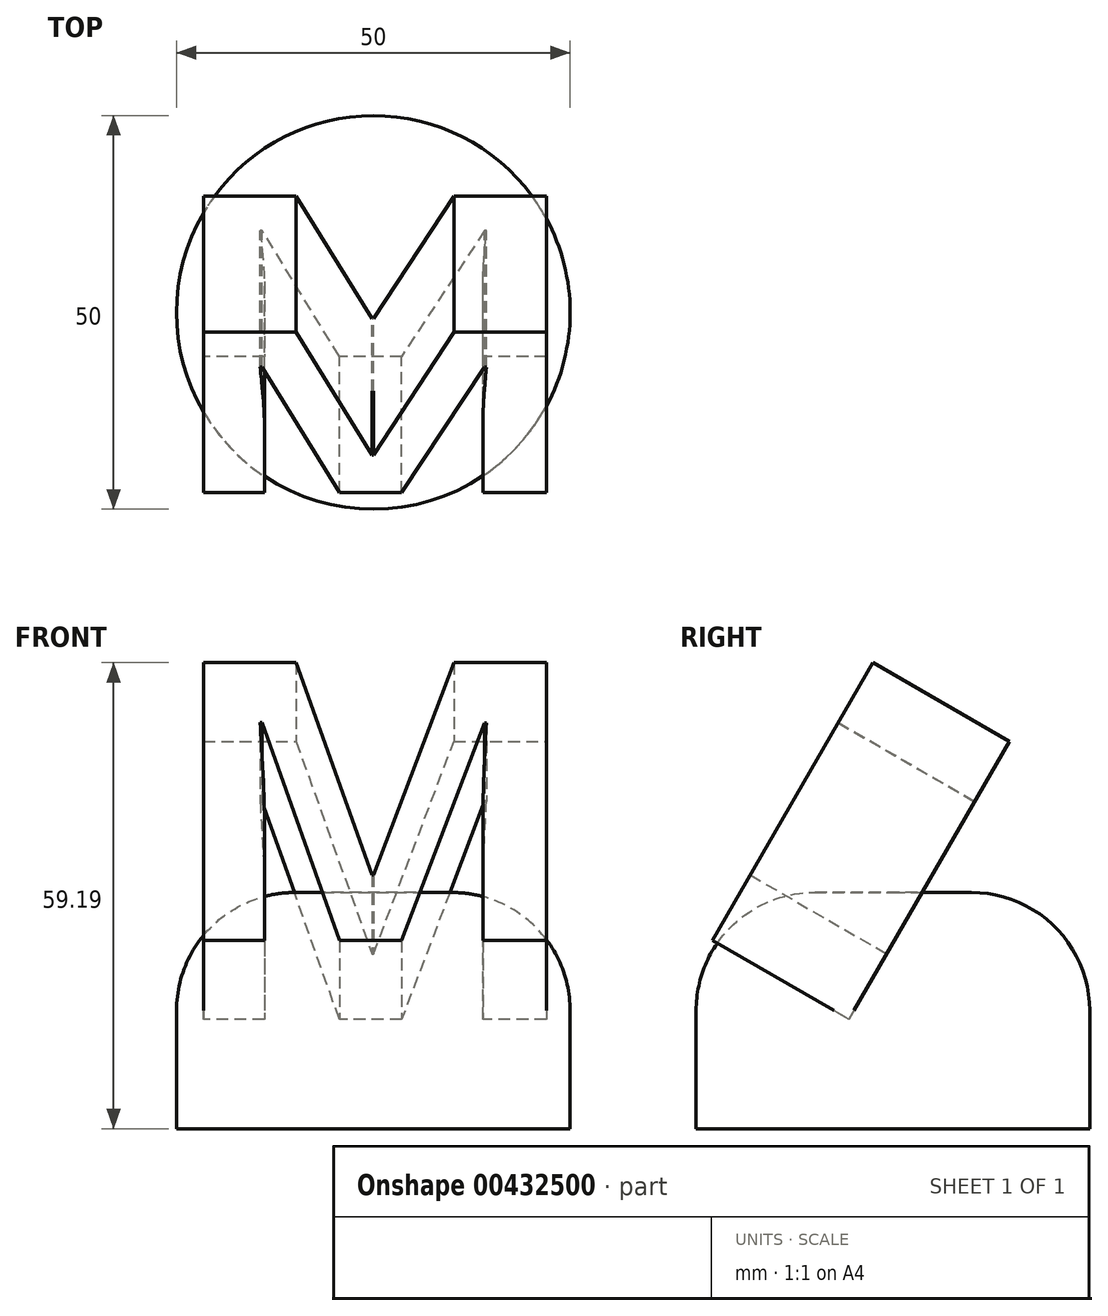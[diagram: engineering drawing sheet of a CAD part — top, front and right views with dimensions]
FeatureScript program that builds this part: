
annotation { "Feature Type Name" : "Feature", "Feature Type Description" : "" }
export const myFeature = defineFeature(function(context is Context, id is Id, definition is map)
    precondition{}
    {
        {
            var Q0;
            Q0=qCreatedBy(makeId("Top.planeOp"),FACE);
            var sketch = newSketch(context, id + "F0", { "sketchPlane" : qUnion([Q0])});
            skText(sketch, "E0", { "text": "M", "fontName": "OpenSans-Bold.ttf"});
            const initialGuessF0  = {"E0": [-0.09905, -0.02287, 1, 0, 0.0411]};
            skSetInitialGuess(sketch, initialGuessF0);
            skSolve(sketch);
        }
        {
            var Q0;
            Q0=qSketchRegion(id+"F0",true);
            extrude(context, id + "F1", {"entities" : qUnion([Q0]), "depth" : 20 * mm});
        }
        {
            var Q0;
            Q0=makeQuery(id+"F1.opExtrude","SWEPT_BODY",BODY,{"disambiguationData":[OSD([sQuery(id+"F0.wireOp",EDGE,"E0.sketch_text.stroke-0"),sQuery(id+"F0.wireOp",EDGE,"E0.sketch_text.stroke-1"),sQuery(id+"F0.wireOp",EDGE,"E0.sketch_text.stroke-2"),sQuery(id+"F0.wireOp",EDGE,"E0.sketch_text.stroke-3"),sQuery(id+"F0.wireOp",EDGE,"E0.sketch_text.stroke-4"),sQuery(id+"F0.wireOp",EDGE,"E0.sketch_text.stroke-5"),sQuery(id+"F0.wireOp",EDGE,"E0.sketch_text.stroke-6"),sQuery(id+"F0.wireOp",EDGE,"E0.sketch_text.stroke-7"),sQuery(id+"F0.wireOp",EDGE,"E0.sketch_text.stroke-8"),sQuery(id+"F0.wireOp",EDGE,"E0.sketch_text.stroke-9"),sQuery(id+"F0.wireOp",EDGE,"E0.sketch_text.stroke-10"),sQuery(id+"F0.wireOp",EDGE,"E0.sketch_text.stroke-11"),sQuery(id+"F0.wireOp",EDGE,"E0.sketch_text.stroke-12"),sQuery(id+"F0.wireOp",EDGE,"E0.sketch_text.stroke-13")])]});
            transform(context, id + "F2", {"entities" : qUnion([Q0]), "transformType" : TransformType.TRANSLATION_3D, "dx" : 76.45 * mm, "dy" : 0 * mm, "dz" : 0 * mm, "makeCopy" : false});
        }
        {
            var Q0;
            Q0=qCreatedBy(makeId("Top.planeOp"),FACE);
            var sketch = newSketch(context, id + "F3", { "sketchPlane" : qUnion([Q0])});
            skCircle(sketch, "E1", {"center": v(-27.2, 27.91) * mm, "radius": 25 * mm});
            skSolve(sketch);
        }
        {
            var Q0;
            Q0=makeQuery(id+"F1.opExtrude","SWEPT_BODY",BODY,{"disambiguationData":[OSD([sQuery(id+"F0.wireOp",EDGE,"E0.sketch_text.stroke-0"),sQuery(id+"F0.wireOp",EDGE,"E0.sketch_text.stroke-1"),sQuery(id+"F0.wireOp",EDGE,"E0.sketch_text.stroke-2"),sQuery(id+"F0.wireOp",EDGE,"E0.sketch_text.stroke-3"),sQuery(id+"F0.wireOp",EDGE,"E0.sketch_text.stroke-4"),sQuery(id+"F0.wireOp",EDGE,"E0.sketch_text.stroke-5"),sQuery(id+"F0.wireOp",EDGE,"E0.sketch_text.stroke-6"),sQuery(id+"F0.wireOp",EDGE,"E0.sketch_text.stroke-7"),sQuery(id+"F0.wireOp",EDGE,"E0.sketch_text.stroke-8"),sQuery(id+"F0.wireOp",EDGE,"E0.sketch_text.stroke-9"),sQuery(id+"F0.wireOp",EDGE,"E0.sketch_text.stroke-10"),sQuery(id+"F0.wireOp",EDGE,"E0.sketch_text.stroke-11"),sQuery(id+"F0.wireOp",EDGE,"E0.sketch_text.stroke-12"),sQuery(id+"F0.wireOp",EDGE,"E0.sketch_text.stroke-13")])]});
            transform(context, id + "F4", {"entities" : qUnion([Q0]), "transformType" : TransformType.TRANSLATION_3D, "dx" : 27.3 * mm, "dy" : 0 * mm, "dz" : 0 * mm, "makeCopy" : false});
        }
        {
            var Q0;
            Q0=makeQuery(id+"F3.imprint","IMPRINT",FACE,{"disambiguationData":[TD([[makeQuery(id+"F3.imprint","IMPRINT",EDGE,{"derivedFrom":sQuery(id+"F3.wireOp",EDGE,"E1")}),1.0]])]});
            extrude(context, id + "F5", {"entities" : qUnion([Q0]), "depth" : 30 * mm});
        }
        {
            var Q0;
            Q0=makeQuery(id+"F5.opExtrude","CAP_FACE",FACE,{"disambiguationData":[OSD([sQuery(id+"F3.wireOp",EDGE,"E1")])],"isStart":false});
            fillet(context, id + "F6", {"entities" : qUnion([Q0]), "radius" : 15 * mm, "tangentPropagation" : true, "allowEdgeOverflow" : false});
        }
        {
            var Q0;
            Q0=makeQuery(id+"F1.opExtrude","SWEPT_BODY",BODY,{"disambiguationData":[OSD([sQuery(id+"F0.wireOp",EDGE,"E0.sketch_text.stroke-0"),sQuery(id+"F0.wireOp",EDGE,"E0.sketch_text.stroke-1"),sQuery(id+"F0.wireOp",EDGE,"E0.sketch_text.stroke-2"),sQuery(id+"F0.wireOp",EDGE,"E0.sketch_text.stroke-3"),sQuery(id+"F0.wireOp",EDGE,"E0.sketch_text.stroke-4"),sQuery(id+"F0.wireOp",EDGE,"E0.sketch_text.stroke-5"),sQuery(id+"F0.wireOp",EDGE,"E0.sketch_text.stroke-6"),sQuery(id+"F0.wireOp",EDGE,"E0.sketch_text.stroke-7"),sQuery(id+"F0.wireOp",EDGE,"E0.sketch_text.stroke-8"),sQuery(id+"F0.wireOp",EDGE,"E0.sketch_text.stroke-9"),sQuery(id+"F0.wireOp",EDGE,"E0.sketch_text.stroke-10"),sQuery(id+"F0.wireOp",EDGE,"E0.sketch_text.stroke-11"),sQuery(id+"F0.wireOp",EDGE,"E0.sketch_text.stroke-12"),sQuery(id+"F0.wireOp",EDGE,"E0.sketch_text.stroke-13")])]});
            var Q1;
            Q1=makeQuery(id+"F1.opExtrude","CAP_EDGE",EDGE,{"disambiguationData":[OSD([sQuery(id+"F0.wireOp",EDGE,"E0.sketch_text.stroke-4")])],"isStart":true});
            transform(context, id + "F7", {"entities" : qUnion([Q0]), "transformType" : TransformType.ROTATION, "transformAxis" : qUnion([Q1]), "angle" : 60 * degree, "oppositeDirection" : true, "makeCopy" : false});
        }
        {
            var Q0;
            Q0=makeQuery(id+"F1.opExtrude","SWEPT_BODY",BODY,{"disambiguationData":[OSD([sQuery(id+"F0.wireOp",EDGE,"E0.sketch_text.stroke-0"),sQuery(id+"F0.wireOp",EDGE,"E0.sketch_text.stroke-1"),sQuery(id+"F0.wireOp",EDGE,"E0.sketch_text.stroke-2"),sQuery(id+"F0.wireOp",EDGE,"E0.sketch_text.stroke-3"),sQuery(id+"F0.wireOp",EDGE,"E0.sketch_text.stroke-4"),sQuery(id+"F0.wireOp",EDGE,"E0.sketch_text.stroke-5"),sQuery(id+"F0.wireOp",EDGE,"E0.sketch_text.stroke-6"),sQuery(id+"F0.wireOp",EDGE,"E0.sketch_text.stroke-7"),sQuery(id+"F0.wireOp",EDGE,"E0.sketch_text.stroke-8"),sQuery(id+"F0.wireOp",EDGE,"E0.sketch_text.stroke-9"),sQuery(id+"F0.wireOp",EDGE,"E0.sketch_text.stroke-10"),sQuery(id+"F0.wireOp",EDGE,"E0.sketch_text.stroke-11"),sQuery(id+"F0.wireOp",EDGE,"E0.sketch_text.stroke-12"),sQuery(id+"F0.wireOp",EDGE,"E0.sketch_text.stroke-13")])]});
            transform(context, id + "F8", {"entities" : qUnion([Q0]), "transformType" : TransformType.TRANSLATION_3D, "dx" : -58.6 * mm, "dy" : 45.2 * mm, "dz" : 13.9 * mm, "makeCopy" : false});
        }
    });
